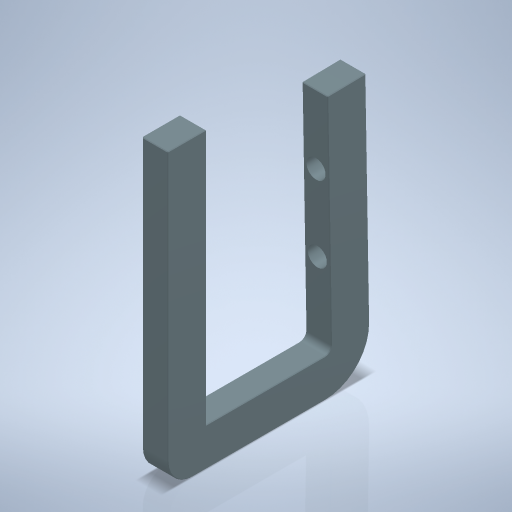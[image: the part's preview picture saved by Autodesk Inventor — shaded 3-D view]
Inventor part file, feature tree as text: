
AUTODESK INVENTOR PART (.ipt)
format: ipt  version: 2024 (Build 280153000, 153)  size: 300,544 bytes
history: native  units: mm
features: sketch x4, plane x1, sweep x1, fillet x1, chamfer x1, hole x1
ambient origin geometry x8: Origin, YZ Plane, XZ Plane, XY Plane, X Axis, Y Axis, Z Axis, Center Point
bodies: Volumenkörper1 (feature_tree)
feature tree (9):
  sketch  "Skizze1"  dims[d0=20.0mm d1=30.0mm d2=215.0mm]
  sketch  "Skizze2"  dims[d3=0.0mm]
  plane  "Arbeitsebene1"
  sweep  "Sweeping1"
  fillet  "Rundung1"  Radius=215.0mm
  chamfer  "Fasen1"  Distance=15.53343mm
  hole  "Bohrung1"  [1 undecoded]
  sketch  "Skizze3"  dims[d4=108.0mm]
  sketch  "Skizze4"  dims[d5=20.0mm d6=15.53343mm d7=0.0mm d8=0.0mm d9=20.0mm d10=170.0mm d11=0.5mm d12=2.0mm d13=45.0deg d14=15.0mm d15=31.75mm d16=4.0mm d17=2.0mm d18=90.0deg d19=8.0mm d20=0.0mm d21=60.0mm d22=54.0mm]
note: 1 required parameter value undecoded (feature->parameter linkage not recoverable at this tier; creation-order binding heuristic only, values carry confidence <= 0.55)
